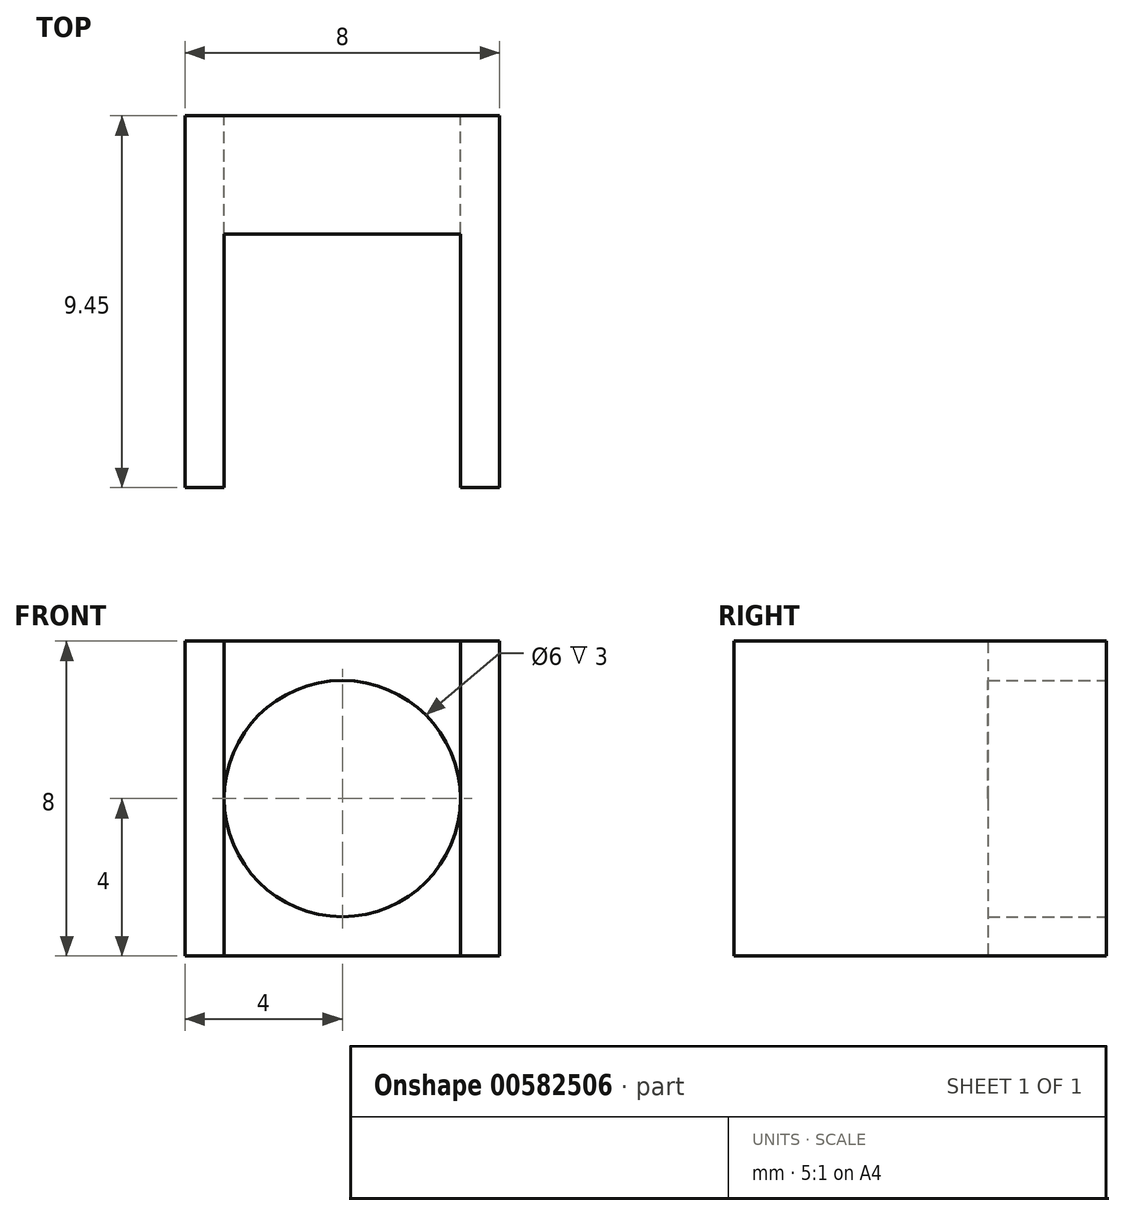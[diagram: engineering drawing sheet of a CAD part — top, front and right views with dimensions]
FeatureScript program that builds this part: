
annotation { "Feature Type Name" : "Feature", "Feature Type Description" : "" }
export const myFeature = defineFeature(function(context is Context, id is Id, definition is map)
    precondition{}
    {
        {
            var Q0;
            Q0=qCreatedBy(makeId("Front.planeOp"),FACE);
            var sketch = newSketch(context, id + "F0", { "sketchPlane" : qUnion([Q0])});
            skCircle(sketch, "E0", {"center": v(0, 0) * mm, "radius": 3 * mm});
            skLineSegment(sketch, "E1.bottom", {"start": v(4, 4) * mm, "end": v(-4, 4) * mm});
            skLineSegment(sketch, "E1.top", {"start": v(4, -4) * mm, "end": v(-4, -4) * mm});
            skLineSegment(sketch, "E1.left", {"start": v(4, 4) * mm, "end": v(4, -4) * mm});
            skLineSegment(sketch, "E1.right", {"start": v(-4, 4) * mm, "end": v(-4, -4) * mm});
            skSolve(sketch);
        }
        {
            var Q0;
            Q0 = qSketchRegion(id + "F0", true);
            extrude(context, id + "F1", {"entities" : qUnion([Q0]), "depth" : 3 * mm, "offsetDistance" : 25 * mm});
        }
        {
            var Q0;
            Q0=makeQuery(id+"F1.opExtrude","CAP_FACE",FACE,{"disambiguationData":[OSD([sQuery(id+"F0.wireOp",EDGE,"E0"),sQuery(id+"F0.wireOp",EDGE,"E1.bottom"),sQuery(id+"F0.wireOp",EDGE,"E1.top"),sQuery(id+"F0.wireOp",EDGE,"E1.left"),sQuery(id+"F0.wireOp",EDGE,"E1.right")])],"isStart":false});
            var sketch = newSketch(context, id + "F2", { "sketchPlane" : qUnion([Q0])});
            skLineSegment(sketch, "E2.bottom", {"start": v(-4, 4) * mm, "end": v(-3, 4) * mm});
            skLineSegment(sketch, "E2.top", {"start": v(-4, -4) * mm, "end": v(-3, -4) * mm});
            skLineSegment(sketch, "E2.left", {"start": v(-4, 4) * mm, "end": v(-4, -4) * mm});
            skLineSegment(sketch, "E2.right", {"start": v(-3, 4) * mm, "end": v(-3, -4) * mm});
            skLineSegment(sketch, "E3.MirrorCS", {"start": v(3, 4) * mm, "end": v(3, -4) * mm});
            skLineSegment(sketch, "E4.MirrorCS", {"start": v(4, 4) * mm, "end": v(3, 4) * mm});
            skLineSegment(sketch, "E5.MirrorCS", {"start": v(4, 4) * mm, "end": v(4, -4) * mm});
            skLineSegment(sketch, "E6.MirrorCS", {"start": v(4, -4) * mm, "end": v(3, -4) * mm});
            skSolve(sketch);
        }
        {
            var Q0;
            Q0 = qSketchRegion(id + "F2", true);
            extrude(context, id + "F3", {"entities" : qUnion([Q0]), "operationType" : NewBodyOperationType.ADD, "depth" : 6.45 * mm, "offsetDistance" : 25 * mm});
        }
    });
